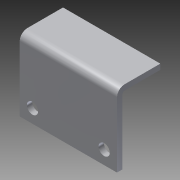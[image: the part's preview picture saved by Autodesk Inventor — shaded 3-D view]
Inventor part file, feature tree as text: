
AUTODESK INVENTOR PART (.ipt)
format: ipt  version: 2013 (Build 170138000, 138)  size: 180,224 bytes
history: native  units: in
note: dims shown in document units (in); Inventor stores cm internally (conversion verified against a paired STEP export)
features: sketch x6, other x6, sheet_metal_op x4, reference x2, extrude x1
ambient origin geometry x8: Origin, YZ Plane, XZ Plane, XY Plane, X Axis, Y Axis, Z Axis, Center Point
bodies: Solid1 (feature_tree)
feature tree (19):
  sheet_metal_op  "Face1"
  sheet_metal_op  "Flange1"
  extrude  "Extrusion1"  Depth=1.5in
  sketch  "Sketch1"  dims[d1=4.297in d2=1.5in]
  other  "Plate1"
  sketch  "Sketch2"  dims[d3=0.295in]
  other  "Plate2"
  sheet_metal_op  "Bend1"
  sheet_metal_op  "Corner1"
  sketch  "Sketch8"  dims[d4=1.181in]
  reference  "Reference1"
  reference  "Reference2"
  sketch  "Sketch10"  dims[d5=0.295in]
  sketch  "Sketch14"  dims[d8=0.125in]
  sketch  "Sketch15"  dims[d9=0.125in d10=0.0625in d11=0.25in d12=0.125in d13=1.0in d14=90.0deg d15=0.05in d16=0.5in d17=0.125in d18=0.125in d19=0.125in d20=0.0in d21=2.0in d22=2.053in d23=1.0in d24=0.0in d29=0.125in d30=0.0in d31=0.125in d32=0.0in d0=1.582in d6=0.0625in d7=0.125in]
  other  "Cut1"
  other  "Cut3"
  other  "Cut4"
  other  "Definition1"
